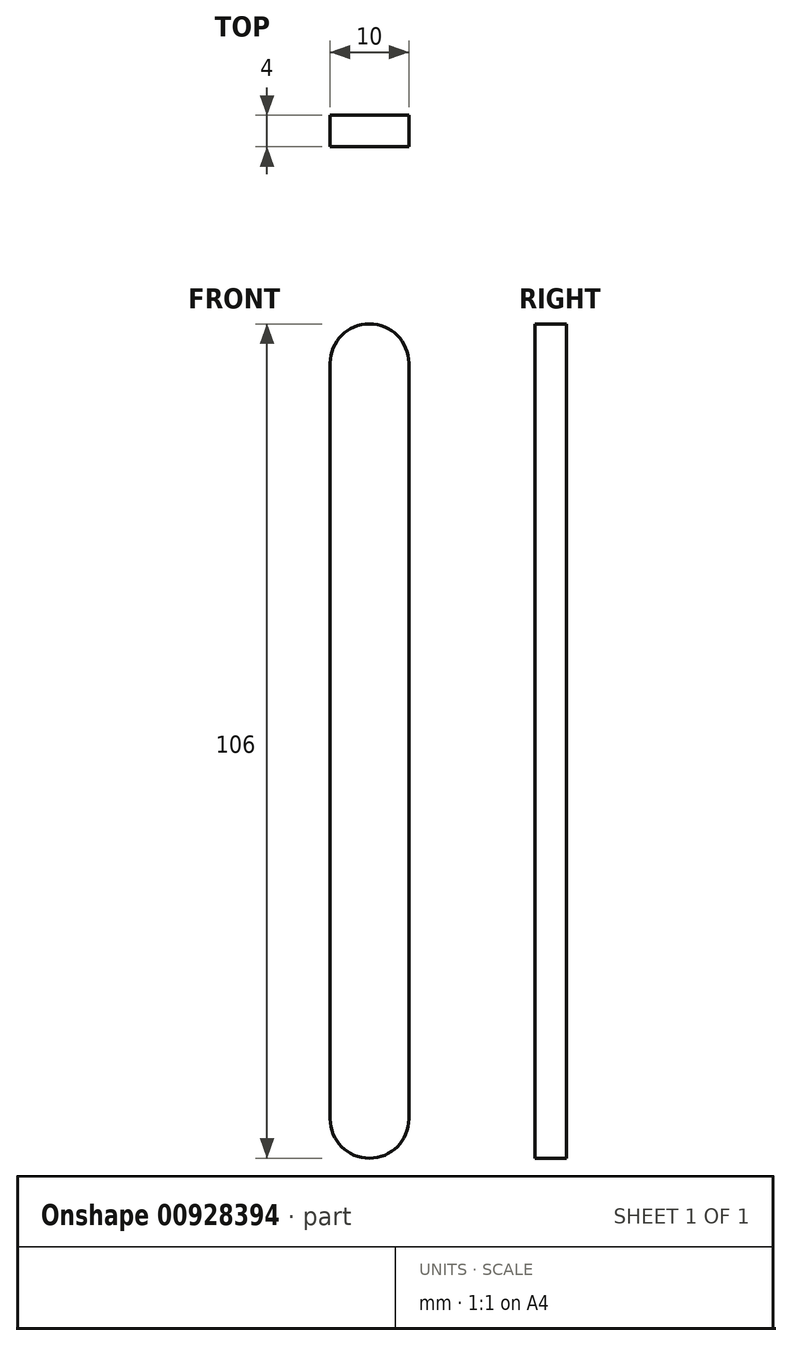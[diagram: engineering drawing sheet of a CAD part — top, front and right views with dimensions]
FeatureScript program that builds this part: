
annotation { "Feature Type Name" : "Feature", "Feature Type Description" : "" }
export const myFeature = defineFeature(function(context is Context, id is Id, definition is map)
    precondition{}
    {
        {
            var Q0;
            Q0=qCreatedBy(makeId("Front.planeOp"),FACE);
            var sketch = newSketch(context, id + "F0", { "sketchPlane" : qUnion([Q0])});
            skLineSegment(sketch, "E0.bottom", {"start": v(92, 230) * mm, "end": v(0, 230) * mm});
            skLineSegment(sketch, "E0.top", {"start": v(92, 0) * mm, "end": v(0, 0) * mm});
            skLineSegment(sketch, "E0.left", {"start": v(92, 230) * mm, "end": v(92, 0) * mm});
            skLineSegment(sketch, "E0.right", {"start": v(0, 230) * mm, "end": v(0, 0) * mm});
            skSolve(sketch);
        }
        {
            var Q0;
            Q0 = qSketchRegion(id + "F0", true);
            extrude(context, id + "F1", {"entities" : qUnion([Q0]), "depth" : 4 * mm, "offsetDistance" : 25 * mm});
        }
        {
            var Q0;
            Q0=makeQuery(id+"F1.opExtrude","CAP_FACE",FACE,{"disambiguationData":[OSD([sQuery(id+"F0.wireOp",EDGE,"E0.bottom"),sQuery(id+"F0.wireOp",EDGE,"E0.top"),sQuery(id+"F0.wireOp",EDGE,"E0.left"),sQuery(id+"F0.wireOp",EDGE,"E0.right")])],"isStart":false});
            var sketch = newSketch(context, id + "F2", { "sketchPlane" : qUnion([Q0])});
            skCircle(sketch, "E1", {"center": v(16, 8) * mm, "radius": 4.5 * mm});
            skCircle(sketch, "E2", {"center": v(76, 8) * mm, "radius": 4.5 * mm});
            skCircle(sketch, "E3", {"center": v(46, 220) * mm, "radius": 6 * mm});
            skSolve(sketch);
        }
        {
            var Q0;
            Q0=sQuery(id+"F2.wireOp",VERTEX,"E1.center");
            var Q1;
            Q1=sQuery(id+"F2.wireOp",VERTEX,"E2.center");
            var Q2;
            Q2=makeQuery(id+"F1.opExtrude","SWEPT_BODY",BODY,{"disambiguationData":[OSD([sQuery(id+"F0.wireOp",EDGE,"E0.bottom"),sQuery(id+"F0.wireOp",EDGE,"E0.top"),sQuery(id+"F0.wireOp",EDGE,"E0.left"),sQuery(id+"F0.wireOp",EDGE,"E0.right")])]});
            hole(context, id + "F3", {"style" : HoleStyle.SIMPLE, "endStyle" : HoleEndStyle.THROUGH, "standardTappedOrClearance" : lookupTablePath({ "standard" : "Custom", "fit" : "Normal", "size" : "M5", "type" : "Clearance" }), "standardBlindInLast" : lookupTablePath({ "fit" : "Normal", "standard" : "Custom", "size" : "M5", "type" : "Clearance" }), "holeDiameter" : 9 * mm, "majorDiameter" : 5 * mm, "isTappedThrough" : true, "tappedDepth" : 12 * mm, "tapClearance" : 3, "locations" : qUnion([Q0, Q1]), "scope" : qUnion([Q2])});
        }
        {
            var Q0;
            Q0=sQuery(id+"F2.wireOp",VERTEX,"E3.center");
            var Q1;
            Q1=makeQuery(id+"F1.opExtrude","SWEPT_BODY",BODY,{"disambiguationData":[OSD([sQuery(id+"F0.wireOp",EDGE,"E0.bottom"),sQuery(id+"F0.wireOp",EDGE,"E0.top"),sQuery(id+"F0.wireOp",EDGE,"E0.left"),sQuery(id+"F0.wireOp",EDGE,"E0.right")])]});
            hole(context, id + "F4", {"style" : HoleStyle.SIMPLE, "endStyle" : HoleEndStyle.THROUGH, "holeDiameter" : 12 * mm, "majorDiameter" : 5 * mm, "isTappedThrough" : true, "tappedDepth" : 12 * mm, "tapClearance" : 3, "locations" : qUnion([Q0]), "scope" : qUnion([Q1])});
        }
        {
            var Q0;
            Q0=makeQuery(id+"F1.opExtrude","CAP_FACE",FACE,{"disambiguationData":[OSD([sQuery(id+"F0.wireOp",EDGE,"E0.bottom"),sQuery(id+"F0.wireOp",EDGE,"E0.top"),sQuery(id+"F0.wireOp",EDGE,"E0.left"),sQuery(id+"F0.wireOp",EDGE,"E0.right")])],"isStart":false});
            var sketch = newSketch(context, id + "F5", { "sketchPlane" : qUnion([Q0])});
            skLineSegment(sketch, "E4", {"start": v(46, 100) * mm, "end": v(46, 196) * mm});
            skArc(sketch, "E5.0.startCap", {"start": v(51, 100) * mm, "mid": v(46, 95) * mm, "end": v(41, 100) * mm});
            skArc(sketch, "E5.0.endCap", {"start": v(41, 196) * mm, "mid": v(46, 201) * mm, "end": v(51, 196) * mm});
            skLineSegment(sketch, "E5.0.left", {"start": v(41, 100) * mm, "end": v(41, 196) * mm});
            skLineSegment(sketch, "E5.0.right", {"start": v(51, 100) * mm, "end": v(51, 196) * mm});
            skSolve(sketch);
        }
        {
            var Q0;
            Q0=makeQuery(id+"F5.imprint","IMPRINT",FACE,{"disambiguationData":[TD([[makeQuery(id+"F5.imprint","IMPRINT",EDGE,{"derivedFrom":sQuery(id+"F5.wireOp",EDGE,"E5.0.startCap")}),-1.0]])]});
            extrude(context, id + "F6", {"entities" : qUnion([Q0]), "operationType" : NewBodyOperationType.REMOVE, "endBound" : BoundingType.UP_TO_NEXT, "oppositeDirection" : true, "depth" : 4 * mm, "offsetDistance" : 25 * mm});
        }
    });
